# Revit family: SNS LED
name_source: partatom
category: Осветительные приборы
revit_build: Autodesk Revit 2016 (Build: 20150714_1515(x64)
units: mm (PartAtom-declared; Revit-internal decimal feet)

## family parameters
Источник света = Нет
Общий = Нет
Основа = Грань
При загрузке вырезать с полостями = Нет
Размер круглого соединителя = Использовать диаметр
Тип детали = Нормальный
Точка расчета площади = Нет

## types (1)
- SNS LED
    1 = Нет
    2 = Нет
    3 = Нет
    4 = Да
    5 = Нет
    6 = Нет
    7 = Нет
    ADSK_Единица измерения = Шт.
    ADSK_Завод-изготовитель = ООО МГК Световые технологии
    ADSK_Классификация нагрузок = Прочее
    ADSK_Количество фаз = 1
    ADSK_Количество фаз числовое = 1
    ADSK_Коэффициент мощности = 0.97
    ADSK_Масса = 0
    ADSK_Наименование = Светодиодный светильник типа CARDAN с возможностью регулирования направления светового потока. Преимуществом серии является наличие четырех вариантов углов рефлектора, от узкого (10 градусов) до широкого (70 градусов), что позволяет благодаря светильникам одного типа реализовывать различные сцены освещения, как общего, так и акцентного
    ADSK_Напряжение = 230 В
    ADSK_Номинальная мощность = 0 кВт
    ADSK_Полная мощность = 0 кВ·А
    ADSK_Размер_Высота = 163 мм
    ADSK_Размер_Длина = 140 мм
    ADSK_Размер_Ширина = 140 мм
    ADSK_Ток = 0 А
    ADSK_Энергоэффективность = 0 лм/Вт
    IP Class = IP20
    URL = http://ltcompany.com
    a = 125 мм
    b = 120 мм
    Блок аварийного питания = Нет
    Выбор ИС 1 = IES SNS LED : SNS LED 1M 30 W D10 4000K
    Выбор ИС 2 = IES SNS LED : SNS LED 1M 30 W D10 4000K
    Выбор ИС 3 = IES SNS LED : SNS LED 1M 30 W D10 4000K
    Выбор ИС 4 = IES SNS LED : SNS LED 1M 30 W D10 4000K
    Выбор ИС 5 = IES SNS LED : SNS LED 1M 30 W D10 4000K
    Выбор ИС 6 = IES SNS LED : SNS LED 1M 30 W D10 4000K
    Выбор ИС 7 = IES SNS LED : SNS LED 1M 30 W D10 4000K
    Группа модели = Светильники
    Изготовитель = ООО МГК Световые технологии
    Класс Защиты = I
    Климатическая зона = УХЛ 4
    Код по классификатору = D5020200
    Корпус = Черный металл
    Корпус лампы = Белый металл
    Область использования = Гипер-/супермаркеты, Гостиницы, Культурно-развлекательные, Магазины/Бутики, Объекты общественного питания, ТРЦ
    Описание = Светодиодный светильник типа CARDAN с возможностью регулирования направления светового потока. Преимуществом серии является наличие четырех вариантов углов рефлектора, от узкого (10 градусов) до широкого (70 градусов), что позволяет благодаря светильникам одного типа реализовывать различные сцены освещения, как общего, так и акцентного
    Отметка по умолчанию = 0 мм
    Плафон = Плафон самосвечение
    Полная установленная мощность = 0 кВ·А
    Тип ИС = LED
    Тип ПРА = Драйвер
    Тип продукции = Светильник

## geometry (parser evidence)
native form markers: Blend x4
no freeform markers — native parametric forms only
